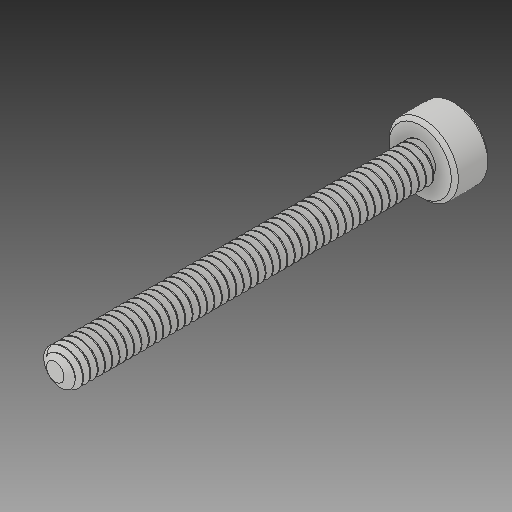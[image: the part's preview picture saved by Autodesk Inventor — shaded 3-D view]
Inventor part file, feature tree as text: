
AUTODESK INVENTOR PART (.ipt)
format: ipt  version: 2018 (Build 220112000, 112)  size: 1,735,168 bytes
history: native  units: in
note: dims shown in document units (in); Inventor stores cm internally (conversion verified against a paired STEP export)
features: chamfer x1
ambient origin geometry x8: Origin, YZ Plane, XZ Plane, XY Plane, X Axis, Y Axis, Z Axis, Center Point
bodies: Solid1 (feature_tree)
feature tree (1):
  chamfer  "Chamfer1"  [1 undecoded]
note: 1 required parameter value undecoded (feature->parameter linkage not recoverable at this tier; creation-order binding heuristic only, values carry confidence <= 0.55)
